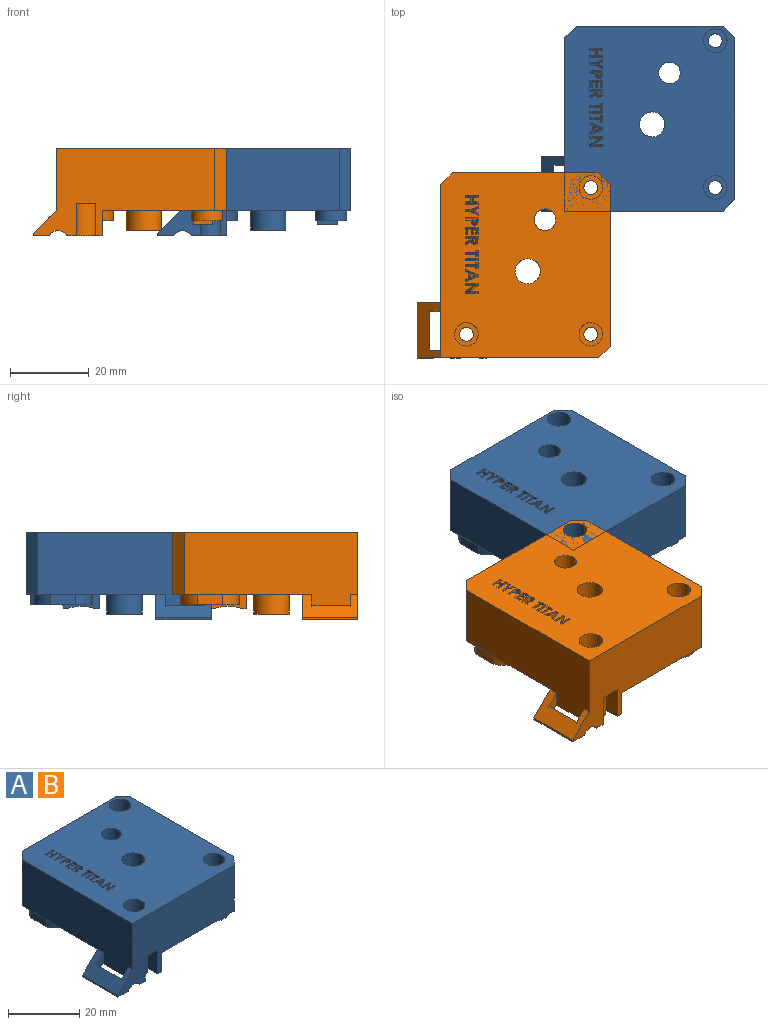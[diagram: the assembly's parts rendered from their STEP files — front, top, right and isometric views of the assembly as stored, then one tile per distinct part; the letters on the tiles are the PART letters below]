
ASSEMBLY  parts=2 mates=1
PART A: 294 faces, bbox 49.3x47.2x22.4 mm
  f0: plane 11.19x5.6mm, normal (1,0,0), area 58.1mm2, adj f2,f4,f7,f9,f56,f57,f58,f59
  f1: plane 47x43.2mm, normal (0,0,-1), area 976.5mm2, adj f6,f8,f9,f17,f18,f31,f32,f33
  f2: plane 5x1.14mm, normal (0,0,-1), area 5.7mm2, adj f0,f5,f57,f59
  f3: cylinder r=1.75mm len=3.5mm, axis (0,0,1), area 37.4mm2, adj f7,f64
  f4: plane 5x1.14mm, normal (0,0,-1), area 5.7mm2, adj f0,f5,f56,f59
  f5: plane 12.96x5.6mm, normal (-1,0,0), area 66.3mm2, adj f2,f4,f7,f8,f56,f57,f58,f59
  f6: plane 5.79x2mm, normal (1,0,0), area 11.6mm2, adj f1,f46,f76,f80
  f7: plane 8x7.9mm, normal (0,0,-1), area 43.6mm2, adj f0,f3,f5,f8,f9,f47,f58
  f8: cylinder r=4mm len=4.74mm, axis (0,0,1), area 23.2mm2, adj f1,f5,f7,f47,f76,f77
  f9: cylinder r=4mm len=6.41mm, axis (0,0,1), area 29.5mm2, adj f0,f1,f7,f47,f75,f76
  f10: plane 11x8.95mm, normal (0,0,-1), area 34.7mm2, adj f17,f20,f24,f26,f27,f35,f38,f39
  f11: plane 0.07x0.06mm, normal (0,0,-1), area 0mm2, adj f12,f25,f35
  f12: plane 0.83x0.07mm, normal (-1,0,0), area 0.1mm2, adj f11,f21,f25,f35
  f13: cylinder r=1.75mm len=4.55mm, axis (0,0,1), area 50mm2, adj f36,f60
  f14: plane 1.54x0.86mm, normal (0,-1,0), area 0.4mm2, adj f15,f16,f22,f23,f29
  f15: cylinder r=4.23mm len=2.14mm, axis (0,1,0), area 3.8mm2, adj f14,f16,f26,f29
  f16: plane 14x4.13mm, normal (0,0,-1), area 40mm2, adj f14,f15,f17,f19,f23,f24,f26,f33
  f17: plane 46.12x22.25mm, normal (0,-1,0), area 685.3mm2, adj f1,f10,f16,f18,f19,f24,f30,f39
  f18: plane 44x19.59mm, normal (-1,0,0), area 732.1mm2, adj f1,f17,f22,f25,f26,f27,f28,f30
  f19: plane 14x0.53mm, normal (-1,0,0), area 7.4mm2, adj f16,f17,f30,f33
  f20: plane 3.01x0.83mm, normal (-1,0,0), area 2.5mm2, adj f10,f21,f35,f38
  f21: plane 10.06x3.6mm, normal (-0.5,0,-0.87), area 39.7mm2, adj f12,f20,f22,f25,f33,f35,f37
  f22: plane 10.06x3.6mm, normal (0.5,0,-0.87), area 17.1mm2, adj f14,f18,f21,f23,f25,f28,f29,f33
  f23: plane 10.06x0.83mm, normal (1,0,0), area 8.3mm2, adj f14,f16,f22,f33
  f24: cylinder r=2.55mm len=4.45mm, axis (0,-1,0), area 9.7mm2, adj f10,f16,f17,f26
  f25: plane 4.09x2.98mm, normal (0,-1,0), area 2mm2, adj f11,f12,f18,f21,f22,f27,f35
  f26: plane 8.09x6.45mm, normal (0,1,0), area 20.8mm2, adj f10,f15,f16,f18,f24,f27,f29,f30
  f27: cylinder r=4.23mm len=4.47mm, axis (0,1,0), area 12.2mm2, adj f10,f18,f25,f26,f35
  f28: plane 5.38x2.76mm, normal (0,-1,0), area 8.8mm2, adj f18,f22,f29,f30
  f29: plane 9.9x2.63mm, normal (1,0,0), area 25mm2, adj f14,f15,f22,f26,f28,f30
  f30: plane 14x5.92mm, normal (-0.71,0,0.71), area 78.6mm2, adj f17,f18,f19,f26,f28,f29,f33
  f31: plane 41x15.8mm, normal (1,0,0), area 647.8mm2, adj f1,f66,f67,f90
  f32: plane 37.2x15.8mm, normal (0,1,0), area 587.8mm2, adj f1,f67,f68,f90
  f33: plane 9.95x6.45mm, normal (0,1,0), area 33.2mm2, adj f1,f16,f19,f21,f22,f23,f30,f37
  f34: cylinder r=1.75mm len=3.5mm, axis (0,0,1), area 37.4mm2, adj f45,f62
  f35: cylinder r=3.25mm len=6.5mm, axis (0,0,-1), area 50.2mm2, adj f10,f11,f12,f20,f21,f25,f27,f36
  f36: plane 6.5x6.5mm, normal (0,0,-1), area 23.6mm2, adj f13,f35
  f37: plane 5.62x3mm, normal (1,0,0), area 16.9mm2, adj f1,f21,f33,f38
  f38: plane 6.45x2.57mm, normal (0,1,0), area 16.6mm2, adj f1,f10,f20,f37,f40
  f39: plane 8.45x6mm, normal (1,0,0), area 44.7mm2, adj f1,f10,f17,f40,f69,f70,f72
  f40: cylinder r=5mm len=6.45mm, axis (0,0,-1), area 50.7mm2, adj f1,f10,f38,f39
  f41: plane 8.25x2.61mm, normal (1,0,0), area 21.5mm2, adj f10,f17,f42,f44
  f42: cylinder r=3.75mm len=8.25mm, axis (0,0,-1), area 48.8mm2, adj f10,f41,f43,f44
  f43: plane 8.25x4.42mm, normal (-1,0,0), area 36.4mm2, adj f10,f17,f42,f44
  f44: plane 5x4.42mm, normal (0,0,-1), area 13.5mm2, adj f17,f41,f42,f43
  f45: plane 8x8mm, normal (0,0,-1), area 40.6mm2, adj f34,f46
  f46: cylinder r=4mm len=8mm, axis (0,0,1), area 83mm2, adj f1,f6,f45,f69,f71,f72,f73,f76
  f47: plane 5.9x2.6mm, normal (0,1,0), area 15.3mm2, adj f1,f7,f8,f9
  f48: plane 6.33x2.6mm, normal (-1,0,0), area 16.5mm2, adj f1,f49,f51
  f49: cylinder r=7.5mm len=15mm, axis (0,0,1), area 105.5mm2, adj f1,f48,f51
  f50: cylinder r=5mm len=10mm, axis (0,0,1), area 125.7mm2, adj f51,f52
  f51: plane 15x14.3mm, normal (0,0,-1), area 95.2mm2, adj f48,f49,f50
  f52: plane 10x10mm, normal (0,0,-1), area 78.5mm2, adj f50
  f53: cylinder r=3.2mm len=20.8mm, axis (0,0,-1), area 418.2mm2, adj f54,f90
  f54: plane 9x9mm, normal (0,0,-1), area 31.4mm2, adj f53,f55
  f55: cylinder r=4.5mm len=9mm, axis (0,0,1), area 157.2mm2, adj f1,f54,f76,f82,f83
  f56: plane 5.6x5mm, normal (0,-1,0), area 28mm2, adj f0,f4,f5,f76
  f57: plane 5x0.5mm, normal (0,1,0), area 2.5mm2, adj f0,f2,f5,f58
  f58: cylinder r=0.5mm len=5mm, axis (1,0,0), area 3.9mm2, adj f0,f5,f7,f57
  f59: cylinder r=10.91mm len=6.91mm, axis (1,0,0), area 35.2mm2, adj f0,f2,f4,f5
  f60: plane 6x6mm, normal (0,0,1), area 18.7mm2, adj f13,f61
  f61: cylinder r=3mm len=15mm, axis (0,0,1), area 282.7mm2, adj f60,f90
  f62: plane 6x6mm, normal (0,0,1), area 18.7mm2, adj f34,f63
  f63: cylinder r=3mm len=15mm, axis (0,0,1), area 282.7mm2, adj f62,f90
  f64: plane 6x6mm, normal (0,0,1), area 18.7mm2, adj f3,f65
  f65: cylinder r=3mm len=15mm, axis (0,0,1), area 282.7mm2, adj f64,f90
  f66: plane 15.8x3mm, normal (0.71,-0.71,0), area 67mm2, adj f1,f17,f31,f90
  f67: plane 15.8x3mm, normal (0.71,0.71,0), area 67mm2, adj f1,f31,f32,f90
  f68: plane 15.8x3mm, normal (-0.71,0.71,0), area 67mm2, adj f1,f18,f32,f90
  f69: plane 23.2x2mm, normal (0,-1,0), area 46.4mm2, adj f1,f39,f46,f72
  f70: plane 26.6x2mm, normal (0,1,0), area 53.2mm2, adj f1,f39,f71,f72
  f71: plane 2x1.1mm, normal (-1,0,0), area 2.2mm2, adj f1,f46,f70,f72
  f72: plane 26.6x3mm, normal (0,0,-1), area 75.2mm2, adj f39,f46,f69,f70,f71
  f73: plane 2x0.1mm, normal (0,1,0), area 0.2mm2, adj f1,f46,f74,f76
  f74: plane 37.3x2mm, normal (-1,0,0), area 74.6mm2, adj f1,f73,f75,f76
  f75: plane 2x0.1mm, normal (0,-1,0), area 0.2mm2, adj f1,f9,f74,f76
  f76: plane 40.1x20.1mm, normal (0,0,-1), area 417.8mm2, adj f0,f5,f6,f8,f9,f46,f55,f56
  f77: plane 12.14x2mm, normal (0,-1,0), area 24.3mm2, adj f1,f8,f76,f81
  f78: plane 17.69x2mm, normal (1,0,0), area 35.4mm2, adj f1,f76,f81,f83
  f79: plane 8.88x2mm, normal (0,1,0), area 17.8mm2, adj f1,f76,f80,f82
  f80: cylinder r=3.5mm len=3.5mm, axis (0,0,-1), area 11mm2, adj f1,f6,f76,f79
  f81: cylinder r=1mm len=2mm, axis (0,0,1), area 3.1mm2, adj f1,f76,f77,f78
  f82: cylinder r=1mm len=2mm, axis (0,0,1), area 3.9mm2, adj f1,f55,f76,f79
  f83: cylinder r=1mm len=2mm, axis (0,0,1), area 2.8mm2, adj f1,f55,f76,f78
  f84: cylinder r=2.75mm len=13.8mm, axis (0,0,1), area 238.4mm2, adj f76,f90
  f85: bspline ~5x1.24mm, area 8.8mm2, adj f86,f90,f110,f112
  f86: bspline ~5x0.84mm, area 5.8mm2, adj f85,f87,f90,f109
  f87: bspline ~5x0.65mm, area 3.3mm2, adj f86,f90,f108,f111
  f88: bspline ~5x1.29mm, area 9mm2, adj f89,f90,f137,f139
  f89: bspline ~5x0.82mm, area 5.5mm2, adj f88,f90,f136,f138
  f90: plane 47x43.2mm, normal (0,0,1), area 1840.3mm2, adj f17,f18,f31,f32,f53,f61,f63,f65
  f91: plane 0.73x0.65mm, normal (0,0,1), area 0.4mm2, adj f92,f93,f94,f95,f96,f97
  f92: plane 1x1mm, normal (0,0.98,0.17), area 0.8mm2, adj f91,f93,f97,f98
  f93: plane 1.01x0.39mm, normal (-0.98,0,0.17), area 0.3mm2, adj f91,f92,f94,f98
  f94: bspline ~1.1x0.73mm, area 0.9mm2, adj f91,f93,f95,f98
  f95: bspline ~1.1x0.45mm, area 0.4mm2, adj f91,f94,f96,f98
  f96: bspline ~1.1x0.5mm, area 0.5mm2, adj f91,f95,f97,f98
  f97: plane 1.01x0.36mm, normal (0.98,0,0.17), area 0.3mm2, adj f91,f92,f96,f98
  f98: plane 2.98x1.67mm, normal (0,0,1), area 1.3mm2, adj f92,f93,f94,f95,f96,f97,f99,f100
  f99: plane 1x0.64mm, normal (-0.98,0,0.17), area 0.6mm2, adj f98,f102,f103,f112
  f100: plane 1.57x1.01mm, normal (0,0.98,0.17), area 1.4mm2, adj f98,f101,f105,f111
  f101: plane 1x0.57mm, normal (0.98,0,0.17), area 0.4mm2, adj f98,f100,f102,f107
  f102: plane 3.18x1mm, normal (0,-0.98,0.17), area 3mm2, adj f98,f99,f101,f106
  f103: bspline ~1.24x1.1mm, area 1.6mm2, adj f98,f99,f104,f110
  f104: bspline ~1.1x0.84mm, area 1.1mm2, adj f98,f103,f105,f109
  f105: bspline ~1.1x0.83mm, area 0.7mm2, adj f98,f100,f104,f108
  f106: plane 10x3.18mm, normal (0,-1,0), area 31.8mm2, adj f90,f102,f107,f112
  f107: plane 10x0.57mm, normal (1,0,0), area 5.7mm2, adj f90,f101,f106,f111
  f108: bspline ~5x0.65mm, area 3.3mm2, adj f87,f105,f109,f111
  f109: bspline ~5x0.84mm, area 5.8mm2, adj f86,f104,f108,f110
  f110: bspline ~5x1.24mm, area 8.8mm2, adj f85,f103,f109,f112
  f111: plane 10x1.38mm, normal (0,1,0), area 13.8mm2, adj f87,f90,f100,f107,f108
  f112: plane 10x0.64mm, normal (-1,0,0), area 6.4mm2, adj f85,f90,f99,f106,f110
  f113: plane 0.82x0.65mm, normal (0,0,1), area 0.5mm2, adj f114,f115,f116,f117,f118
  f114: plane 1x1mm, normal (0,0.98,0.17), area 0.8mm2, adj f113,f115,f118,f119
  f115: plane 1.01x0.41mm, normal (-0.98,0,0.17), area 0.3mm2, adj f113,f114,f116,f119
  f116: bspline ~1.1x0.79mm, area 0.9mm2, adj f113,f115,f117,f119
  f117: bspline ~1.1x0.82mm, area 0.9mm2, adj f113,f116,f118,f119
  f118: plane 1.01x0.39mm, normal (0.98,0,0.17), area 0.3mm2, adj f113,f114,f117,f119
  f119: plane 2.99x1.81mm, normal (0,0,1), area 1.7mm2, adj f114,f115,f116,f117,f118,f120,f121,f122
  f120: plane 1x0.66mm, normal (-0.98,0,0.17), area 0.6mm2, adj f119,f127,f128,f139
  f121: plane 1.55x1mm, normal (-0.44,0.88,0.17), area 1.6mm2, adj f119,f122,f129,f138
  f122: plane 1x0.63mm, normal (0.98,0,0.17), area 0.4mm2, adj f119,f121,f123,f135
  f123: plane 1.56x1mm, normal (0.44,-0.88,0.17), area 1.6mm2, adj f119,f122,f124,f134
  f124: plane 1x0.48mm, normal (0.98,0,0.17), area 0.3mm2, adj f119,f123,f125,f133
  f125: plane 1.56x1mm, normal (0,0.98,0.17), area 1.4mm2, adj f119,f124,f126,f132
  f126: plane 1x0.57mm, normal (0.98,0,0.17), area 0.4mm2, adj f119,f125,f127,f131
  f127: plane 3.18x1mm, normal (0,-0.98,0.17), area 3mm2, adj f119,f120,f126,f130
  f128: bspline ~1.29x1mm, area 1.7mm2, adj f119,f120,f129,f137
  f129: bspline ~1.1x0.9mm, area 1.1mm2, adj f119,f121,f128,f136
  f130: plane 10x3.18mm, normal (0,-1,0), area 31.8mm2, adj f90,f127,f131,f139
  f131: plane 10x0.57mm, normal (1,0,0), area 5.7mm2, adj f90,f126,f130,f132
  f132: plane 10x1.38mm, normal (0,1,0), area 13.8mm2, adj f90,f125,f131,f133
  f133: plane 10x0.19mm, normal (1,0,0), area 1.9mm2, adj f90,f124,f132,f134
  f134: plane 10x1.38mm, normal (0.45,-0.89,0), area 15.5mm2, adj f90,f123,f133,f135
  f135: plane 10x0.63mm, normal (1,0,0), area 6.3mm2, adj f90,f122,f134,f138
  f136: bspline ~5x0.82mm, area 5.5mm2, adj f89,f129,f137,f138
  f137: bspline ~5x1.29mm, area 9mm2, adj f88,f128,f136,f139
  f138: plane 10x1.45mm, normal (-0.45,0.89,0), area 16.2mm2, adj f89,f90,f121,f135,f136
  f139: plane 10x0.66mm, normal (-1,0,0), area 6.6mm2, adj f88,f90,f120,f130,f137
  f140: plane 2.82x1.83mm, normal (0,0,1), area 1mm2, adj f141,f142,f143,f144,f145,f146,f147,f148
  f141: plane 1x0.63mm, normal (-0.98,0,0.17), area 0.4mm2, adj f140,f142,f149,f158
  f142: plane 1.5x1mm, normal (-0.45,0.88,0.17), area 1.4mm2, adj f140,f141,f143,f157
  f143: plane 1.5x1mm, normal (-0.45,-0.88,0.17), area 1.4mm2, adj f140,f142,f144,f156
  f144: plane 1x0.63mm, normal (-0.98,0,0.17), area 0.4mm2, adj f140,f143,f145,f155
  f145: plane 1.8x1.09mm, normal (0.45,0.88,0.17), area 1.9mm2, adj f140,f144,f146,f154
  f146: plane 1.42x1mm, normal (0,0.98,0.17), area 1.3mm2, adj f140,f145,f147,f153
  f147: plane 1x0.57mm, normal (0.98,0,0.17), area 0.4mm2, adj f140,f146,f148,f152
  f148: plane 1.42x1mm, normal (0,-0.98,0.17), area 1.3mm2, adj f140,f147,f149,f151
  f149: plane 1.8x1.09mm, normal (0.45,-0.88,0.17), area 1.9mm2, adj f140,f141,f148,f150
  f150: plane 10x1.8mm, normal (0.45,-0.89,0), area 20.2mm2, adj f90,f149,f151,f158
  f151: plane 10x1.38mm, normal (0,-1,0), area 13.8mm2, adj f90,f148,f150,f152
  f152: plane 10x0.57mm, normal (1,0,0), area 5.7mm2, adj f90,f147,f151,f153
  f153: plane 10x1.38mm, normal (0,1,0), area 13.8mm2, adj f90,f146,f152,f154
  f154: plane 10x1.8mm, normal (0.45,0.89,0), area 20.2mm2, adj f90,f145,f153,f155
  f155: plane 10x0.63mm, normal (-1,0,0), area 6.3mm2, adj f90,f144,f154,f156
  f156: plane 10x1.11mm, normal (-0.45,-0.89,0), area 12.5mm2, adj f90,f143,f155,f157
  f157: plane 10x1.11mm, normal (-0.45,0.89,0), area 12.5mm2, adj f90,f142,f156,f158
  f158: plane 10x0.63mm, normal (-1,0,0), area 6.3mm2, adj f90,f141,f150,f157
  f159: plane 2.82x1.36mm, normal (0,0,1), area 0.9mm2, adj f160,f161,f162,f163,f164,f165,f166,f167
  f160: plane 1.71x1mm, normal (-0.98,0,0.17), area 1.6mm2, adj f159,f161,f167,f175
  f161: plane 1x0.57mm, normal (0,0.98,0.17), area 0.4mm2, adj f159,f160,f162,f174
  f162: plane 1x0.75mm, normal (0.98,0,0.17), area 0.6mm2, adj f159,f161,f163,f173
  f163: plane 2.78x1mm, normal (0,0.98,0.17), area 2.6mm2, adj f159,f162,f164,f172
  f164: plane 1x0.57mm, normal (0.98,0,0.17), area 0.4mm2, adj f159,f163,f165,f171
  f165: plane 2.78x1mm, normal (0,-0.98,0.17), area 2.6mm2, adj f159,f164,f166,f170
  f166: plane 1x0.75mm, normal (0.98,0,0.17), area 0.6mm2, adj f159,f165,f167,f169
  f167: plane 1x0.57mm, normal (0,-0.98,0.17), area 0.4mm2, adj f159,f160,f166,f168
  f168: plane 10x0.57mm, normal (0,-1,0), area 5.7mm2, adj f90,f167,f169,f175
  f169: plane 10x0.57mm, normal (1,0,0), area 5.7mm2, adj f90,f166,f168,f170
  f170: plane 10x2.61mm, normal (0,-1,0), area 26.1mm2, adj f90,f165,f169,f171
  f171: plane 10x0.57mm, normal (1,0,0), area 5.7mm2, adj f90,f164,f170,f172
  f172: plane 10x2.61mm, normal (0,1,0), area 26.1mm2, adj f90,f163,f171,f173
  f173: plane 10x0.57mm, normal (1,0,0), area 5.7mm2, adj f90,f162,f172,f174
  f174: plane 10x0.57mm, normal (0,1,0), area 5.7mm2, adj f90,f161,f173,f175
  f175: plane 10x1.71mm, normal (-1,0,0), area 17.1mm2, adj f90,f160,f168,f174
  f176: plane 2.82x0.22mm, normal (0,0,1), area 0.6mm2, adj f177,f178,f179,f180
  f177: plane 1x0.57mm, normal (-0.98,0,0.17), area 0.4mm2, adj f176,f178,f180,f184
  f178: plane 3.18x1mm, normal (0,0.98,0.17), area 3mm2, adj f176,f177,f179,f183
  f179: plane 1x0.57mm, normal (0.98,0,0.17), area 0.4mm2, adj f176,f178,f180,f182
  f180: plane 3.18x1mm, normal (0,-0.98,0.17), area 3mm2, adj f176,f177,f179,f181
  f181: plane 10x3.18mm, normal (0,-1,0), area 31.8mm2, adj f90,f180,f182,f184
  f182: plane 10x0.57mm, normal (1,0,0), area 5.7mm2, adj f90,f179,f181,f183
  f183: plane 10x3.18mm, normal (0,1,0), area 31.8mm2, adj f90,f178,f182,f184
  f184: plane 10x0.57mm, normal (-1,0,0), area 5.7mm2, adj f90,f177,f181,f183
  f185: plane 2.82x1.36mm, normal (0,0,1), area 0.9mm2, adj f186,f187,f188,f189,f190,f191,f192,f193
  f186: plane 1.71x1mm, normal (-0.98,0,0.17), area 1.6mm2, adj f185,f187,f193,f201
  f187: plane 1x0.57mm, normal (0,0.98,0.17), area 0.4mm2, adj f185,f186,f188,f200
  f188: plane 1x0.75mm, normal (0.98,0,0.17), area 0.6mm2, adj f185,f187,f189,f199
  f189: plane 2.78x1mm, normal (0,0.98,0.17), area 2.6mm2, adj f185,f188,f190,f198
  f190: plane 1x0.57mm, normal (0.98,0,0.17), area 0.4mm2, adj f185,f189,f191,f197
  f191: plane 2.78x1mm, normal (0,-0.98,0.17), area 2.6mm2, adj f185,f190,f192,f196
  f192: plane 1x0.75mm, normal (0.98,0,0.17), area 0.6mm2, adj f185,f191,f193,f195
  f193: plane 1x0.57mm, normal (0,-0.98,0.17), area 0.4mm2, adj f185,f186,f192,f194
  f194: plane 10x0.57mm, normal (0,-1,0), area 5.7mm2, adj f90,f193,f195,f201
  f195: plane 10x0.57mm, normal (1,0,0), area 5.7mm2, adj f90,f192,f194,f196
  f196: plane 10x2.61mm, normal (0,-1,0), area 26.1mm2, adj f90,f191,f195,f197
  f197: plane 10x0.57mm, normal (1,0,0), area 5.7mm2, adj f90,f190,f196,f198
  f198: plane 10x2.61mm, normal (0,1,0), area 26.1mm2, adj f90,f189,f197,f199
  f199: plane 10x0.57mm, normal (1,0,0), area 5.7mm2, adj f90,f188,f198,f200
  f200: plane 10x0.57mm, normal (0,1,0), area 5.7mm2, adj f90,f187,f199,f201
  f201: plane 10x1.71mm, normal (-1,0,0), area 17.1mm2, adj f90,f186,f194,f200
  f202: plane 1.1x0.95mm, normal (0,0,1), area 0.5mm2, adj f203,f204,f205
  f203: plane 1.72x1mm, normal (0.39,0.9,0.17), area 1.6mm2, adj f202,f204,f205,f206
  f204: plane 1.49x1mm, normal (-0.98,0,0.17), area 1.2mm2, adj f202,f203,f205,f206
  f205: plane 1.72x1mm, normal (0.39,-0.9,0.17), area 1.6mm2, adj f202,f203,f204,f206
  f206: plane 2.82x2.57mm, normal (0,0,1), area 1.5mm2, adj f203,f204,f205,f207,f208,f209,f210,f211
  f207: plane 1x0.53mm, normal (-0.98,0,0.17), area 0.4mm2, adj f206,f208,f214,f222
  f208: plane 3.18x1.4mm, normal (-0.37,0.91,0.17), area 3.3mm2, adj f206,f207,f209,f221
  f209: plane 1x0.61mm, normal (0.98,0,0.17), area 0.4mm2, adj f206,f208,f210,f220
  f210: plane 1x0.83mm, normal (0.35,-0.92,0.17), area 0.7mm2, adj f206,f209,f211,f219
  f211: plane 1.63x1mm, normal (0.98,0,0.17), area 1.5mm2, adj f206,f210,f212,f218
  f212: plane 1x0.83mm, normal (0.35,0.92,0.17), area 0.7mm2, adj f206,f211,f213,f217
  f213: plane 1x0.61mm, normal (0.98,0,0.17), area 0.4mm2, adj f206,f212,f214,f216
  f214: plane 3.18x1.4mm, normal (-0.37,-0.91,0.17), area 3.3mm2, adj f206,f207,f213,f215
  f215: plane 10x3.18mm, normal (-0.37,-0.93,0), area 34.2mm2, adj f90,f214,f216,f222
  f216: plane 10x0.61mm, normal (1,0,0), area 6.1mm2, adj f90,f213,f215,f217
  f217: plane 10x0.65mm, normal (0.35,0.94,0), area 7mm2, adj f90,f212,f216,f218
  f218: plane 10x1.38mm, normal (1,0,0), area 13.8mm2, adj f90,f211,f217,f219
  f219: plane 10x0.65mm, normal (0.35,-0.94,0), area 7mm2, adj f90,f210,f218,f220
  f220: plane 10x0.61mm, normal (1,0,0), area 6.1mm2, adj f90,f209,f219,f221
  f221: plane 10x3.18mm, normal (-0.37,0.93,0), area 34.2mm2, adj f90,f208,f220,f222
  f222: plane 10x0.53mm, normal (-1,0,0), area 5.3mm2, adj f90,f207,f215,f221
  f223: plane 2.82x1.89mm, normal (0,0,1), area 1.5mm2, adj f224,f225,f226,f227,f228,f229,f230,f231
  f224: plane 1x0.57mm, normal (-0.98,0,0.17), area 0.4mm2, adj f223,f225,f235,f247
  f225: plane 1.4x1mm, normal (0,0.98,0.17), area 1.2mm2, adj f223,f224,f226,f246
  f226: plane 1.45x1mm, normal (-0.98,0,0.17), area 1.3mm2, adj f223,f225,f227,f245
  f227: plane 1.4x1mm, normal (0,-0.98,0.17), area 1.2mm2, adj f223,f226,f228,f244
  f228: plane 1x0.57mm, normal (-0.98,0,0.17), area 0.4mm2, adj f223,f227,f229,f243
  f229: plane 3.18x1mm, normal (0,0.98,0.17), area 3mm2, adj f223,f228,f230,f242
  f230: plane 1x0.57mm, normal (0.98,0,0.17), area 0.4mm2, adj f223,f229,f231,f241
  f231: plane 1.56x1mm, normal (0,-0.98,0.17), area 1.4mm2, adj f223,f230,f232,f240
  f232: plane 1.45x1mm, normal (0.98,0,0.17), area 1.3mm2, adj f223,f231,f233,f239
  f233: plane 1.56x1mm, normal (0,0.98,0.17), area 1.4mm2, adj f223,f232,f234,f238
  f234: plane 1x0.57mm, normal (0.98,0,0.17), area 0.4mm2, adj f223,f233,f235,f237
  f235: plane 3.18x1mm, normal (0,-0.98,0.17), area 3mm2, adj f223,f224,f234,f236
  f236: plane 10x3.18mm, normal (0,-1,0), area 31.8mm2, adj f90,f235,f237,f247
  f237: plane 10x0.57mm, normal (1,0,0), area 5.7mm2, adj f90,f234,f236,f238
  f238: plane 10x1.38mm, normal (0,1,0), area 13.8mm2, adj f90,f233,f237,f239
  f239: plane 10x1.1mm, normal (1,0,0), area 11mm2, adj f90,f232,f238,f240
  f240: plane 10x1.38mm, normal (0,-1,0), area 13.8mm2, adj f90,f231,f239,f241
  f241: plane 10x0.57mm, normal (1,0,0), area 5.7mm2, adj f90,f230,f240,f242
  f242: plane 10x3.18mm, normal (0,1,0), area 31.8mm2, adj f90,f229,f241,f243
  f243: plane 10x0.57mm, normal (-1,0,0), area 5.7mm2, adj f90,f228,f242,f244
  f244: plane 10x1.22mm, normal (0,-1,0), area 12.2mm2, adj f90,f227,f243,f245
  f245: plane 10x1.1mm, normal (-1,0,0), area 11mm2, adj f90,f226,f244,f246
  f246: plane 10x1.22mm, normal (0,1,0), area 12.2mm2, adj f90,f225,f245,f247
  f247: plane 10x0.57mm, normal (-1,0,0), area 5.7mm2, adj f90,f224,f236,f246
  f248: plane 2.82x2.17mm, normal (0,0,1), area 1.9mm2, adj f249,f250,f251,f252,f253,f254,f255,f256
  f249: plane 1x0.51mm, normal (-0.98,0,0.17), area 0.4mm2, adj f248,f250,f258,f268
  f250: plane 2.66x1.71mm, normal (-0.56,0.81,0.17), area 2.8mm2, adj f248,f249,f251,f267
  f251: plane 2.66x1mm, normal (0,-0.98,0.17), area 2.3mm2, adj f248,f250,f252,f266
  f252: plane 1x0.57mm, normal (-0.98,0,0.17), area 0.4mm2, adj f248,f251,f253,f265
  f253: plane 3.18x1mm, normal (0,0.98,0.17), area 3mm2, adj f248,f252,f254,f264
  f254: plane 1x0.52mm, normal (0.98,0,0.17), area 0.4mm2, adj f248,f253,f255,f263
  f255: plane 2.65x1.71mm, normal (0.56,-0.81,0.17), area 2.8mm2, adj f248,f254,f256,f262
  f256: plane 2.65x1mm, normal (0,0.98,0.17), area 2.3mm2, adj f248,f255,f257,f261
  f257: plane 1x0.57mm, normal (0.98,0,0.17), area 0.4mm2, adj f248,f256,f258,f260
  f258: plane 3.18x1mm, normal (0,-0.98,0.17), area 3mm2, adj f248,f249,f257,f259
  f259: plane 10x3.18mm, normal (0,-1,0), area 31.8mm2, adj f90,f258,f260,f268
  f260: plane 10x0.57mm, normal (1,0,0), area 5.7mm2, adj f90,f257,f259,f261
  f261: plane 10x2.08mm, normal (0,1,0), area 20.8mm2, adj f90,f256,f260,f262
  f262: plane 10x2.08mm, normal (0.57,-0.82,0), area 25.3mm2, adj f90,f255,f261,f263
  f263: plane 10x0.52mm, normal (1,0,0), area 5.2mm2, adj f90,f254,f262,f264
  f264: plane 10x3.18mm, normal (0,1,0), area 31.8mm2, adj f90,f253,f263,f265
  f265: plane 10x0.57mm, normal (-1,0,0), area 5.7mm2, adj f90,f252,f264,f266
  f266: plane 10x2.09mm, normal (0,-1,0), area 20.9mm2, adj f90,f251,f265,f267
  f267: plane 10x2.09mm, normal (-0.57,0.82,0), area 25.4mm2, adj f90,f250,f266,f268
  f268: plane 10x0.51mm, normal (-1,0,0), area 5.1mm2, adj f90,f249,f259,f267
  f269: plane 2.82x1.36mm, normal (0,0,1), area 1.4mm2, adj f270,f271,f272,f273,f274,f275,f276,f277
  f270: plane 1.71x1mm, normal (-0.98,0,0.17), area 1.6mm2, adj f269,f271,f281,f293
  f271: plane 1x0.57mm, normal (0,0.98,0.17), area 0.4mm2, adj f269,f270,f272,f292
  f272: plane 1.32x1mm, normal (0.98,0,0.17), area 1.2mm2, adj f269,f271,f273,f291
  f273: plane 1x0.96mm, normal (0,0.98,0.17), area 0.8mm2, adj f269,f272,f274,f290
  f274: plane 1.32x1mm, normal (-0.98,0,0.17), area 1.2mm2, adj f269,f273,f275,f289
  f275: plane 1x0.57mm, normal (0,0.98,0.17), area 0.4mm2, adj f269,f274,f276,f288
  f276: plane 1.32x1mm, normal (0.98,0,0.17), area 1.2mm2, adj f269,f275,f277,f287
  f277: plane 1.21x1mm, normal (0,0.98,0.17), area 1mm2, adj f269,f276,f278,f286
  f278: plane 1.32x1mm, normal (-0.98,0,0.17), area 1.2mm2, adj f269,f277,f279,f285
  f279: plane 1x0.57mm, normal (0,0.98,0.17), area 0.4mm2, adj f269,f278,f280,f284
  f280: plane 1.71x1mm, normal (0.98,0,0.17), area 1.6mm2, adj f269,f279,f281,f283
  f281: plane 3.18x1mm, normal (0,-0.98,0.17), area 3mm2, adj f269,f270,f280,f282
  f282: plane 10x3.18mm, normal (0,-1,0), area 31.8mm2, adj f90,f281,f283,f293
  f283: plane 10x1.71mm, normal (1,0,0), area 17.1mm2, adj f90,f280,f282,f284
  f284: plane 10x0.57mm, normal (0,1,0), area 5.7mm2, adj f90,f279,f283,f285
  f285: plane 10x1.14mm, normal (-1,0,0), area 11.4mm2, adj f90,f278,f284,f286
  f286: plane 10x0.86mm, normal (0,1,0), area 8.5mm2, adj f90,f277,f285,f287
  f287: plane 10x1.14mm, normal (1,0,0), area 11.4mm2, adj f90,f276,f286,f288
  f288: plane 10x0.57mm, normal (0,1,0), area 5.7mm2, adj f90,f275,f287,f289
  f289: plane 10x1.14mm, normal (-1,0,0), area 11.4mm2, adj f90,f274,f288,f290
  f290: plane 10x0.61mm, normal (0,1,0), area 6.1mm2, adj f90,f273,f289,f291
  f291: plane 10x1.14mm, normal (1,0,0), area 11.4mm2, adj f90,f272,f290,f292
  f292: plane 10x0.57mm, normal (0,1,0), area 5.7mm2, adj f90,f271,f291,f293
  f293: plane 10x1.71mm, normal (-1,0,0), area 17.1mm2, adj f90,f270,f282,f292
PART B: same geometry as A
PLACE A rot(axis=(0,0,1),0deg) t=(37.9,51.62,-1.46)mm
PLACE B t=(6.3,14.32,-1.46)mm fixed
MATE parallel A.f31 <-> B.f31  axis (1,0,0) through (81.1,8.32,6.44)mm
